# Revit family: Balcony roof window FAKRO FGH-V P5 Galeria
name_source: partatom
category: Okna
revit_build: Autodesk Revit 2015 (Build: 20140606_1530(x64)
units: mm (PartAtom-declared; Revit-internal decimal feet)

## types (2) — shared parameters
Apron Material = Fakro - aluminium RAL7022
Bimobject Category = Windows - Roof Windows
CSI MasterFormat 2016 Code = 08 60 00
CSI MasterFormat 2016 Title = Roof Windows and Skylights
CSI UniFormat II Code = B3020
CSI UniFormat II Title = Roof Openings
Glazing = Fakro – Glass
Handle Material = Fakro – handle
IFC Classification = Window
Kod zespołu = B3020110
Material External = Fakro - aluminium RAL7022
Material Internal = Fakro – frame – pinewood
Model = FGH-V P2 Galeria
NBS Reference = 59-72
NBS Reference Description = Roof Window Units
Opis = Balcony roof window
Producent = FAKRO
UNSPC Category = Roofing accessories
UNSPC Code = 301516
URL = www.fakro.com
UV radiation EN 14351-1:2006+A1:2010 = 0.01
Uniclass 1.4 Code = JL11
Uniclass 1.4 Description = Rooflights/Roof windows
Uniclass 2.0 Code = PR-59-72
Uniclass 2.0 Description = Roof Window Units
Uniclass 2015 Code = Pr_30_59_72_77
Uniclass 2015 Title = Skylights
Uw [W/m2K] EN 14351-1:2006+A1:2010 for window dimension 0,94x2,55 m = 1.1
Wysokość = 2545 mm  [stored 8.34974 ft]
air inlet = V40P
air inlet efficiency - 10Pa = 27 m³/h
air permeability class EN 14351-1:2006+A1:2010 = 3
colour = Natural – pine
glass structure = 4HS-10-4HT-8-33.2T
glazing U-value [W/m2K] EN 14351-1:2006+A1:2010 = 0.5
impact resistance class EN 14351-1:2006+A1:2010 = 3
light transmittance factor tv EN 14351-1:2006+A1:2010 = 0.63
material = pinewood
opening method = Balcony window
operation mode = manual
reaction to fire EN 14351-1:2006+A1:2010 = D-s2,d2
resistance to snow load EN 14351-1:2006+A1:2010 = 4H-10-4H-8-33.2
resistance to wind load EN 14351-1:2006+A1:2010 = C4
roof angle = 45-55
solar factor [ g] EN 14351-1:2006+A1:2010 = 0.48
watertightness / unshielded (A) EN 14351-1:2006+A1:2010 = E900
window acoustic performance Rw [dB] EN 14351-1:2006+A1:2010 = 34(-1;-4)

## per-type parameters (varying)
| type | Obj Type | Szerokość | frame area | glass perimeter | glazing area | window internal area | window perimeter | window weight |
| FAKRO FGH-V P5 - CD - 78x255 | 1 mm  [stored 0.00328084 ft] | 777 mm  [stored 2.54921 ft] | 0.67 m² | 7168 mm | 1.32 m² | 1.8 m² | 6644 mm | 113.00 kg |
| FAKRO FGH-V P5 - DD - 94x255 | 2 mm  [stored 0.00656168 ft] | 937 mm | 0.73 m² | 7808 mm | 1.67 m² | 2.04 m² | 6964 mm | 129.00 kg |

note: [stored X ft] marks values corroborated as IEEE doubles in the binary element streams (Revit-internal decimal feet)

## geometry (parser evidence)
native form markers: Sweep x1
no freeform markers — native parametric forms only
